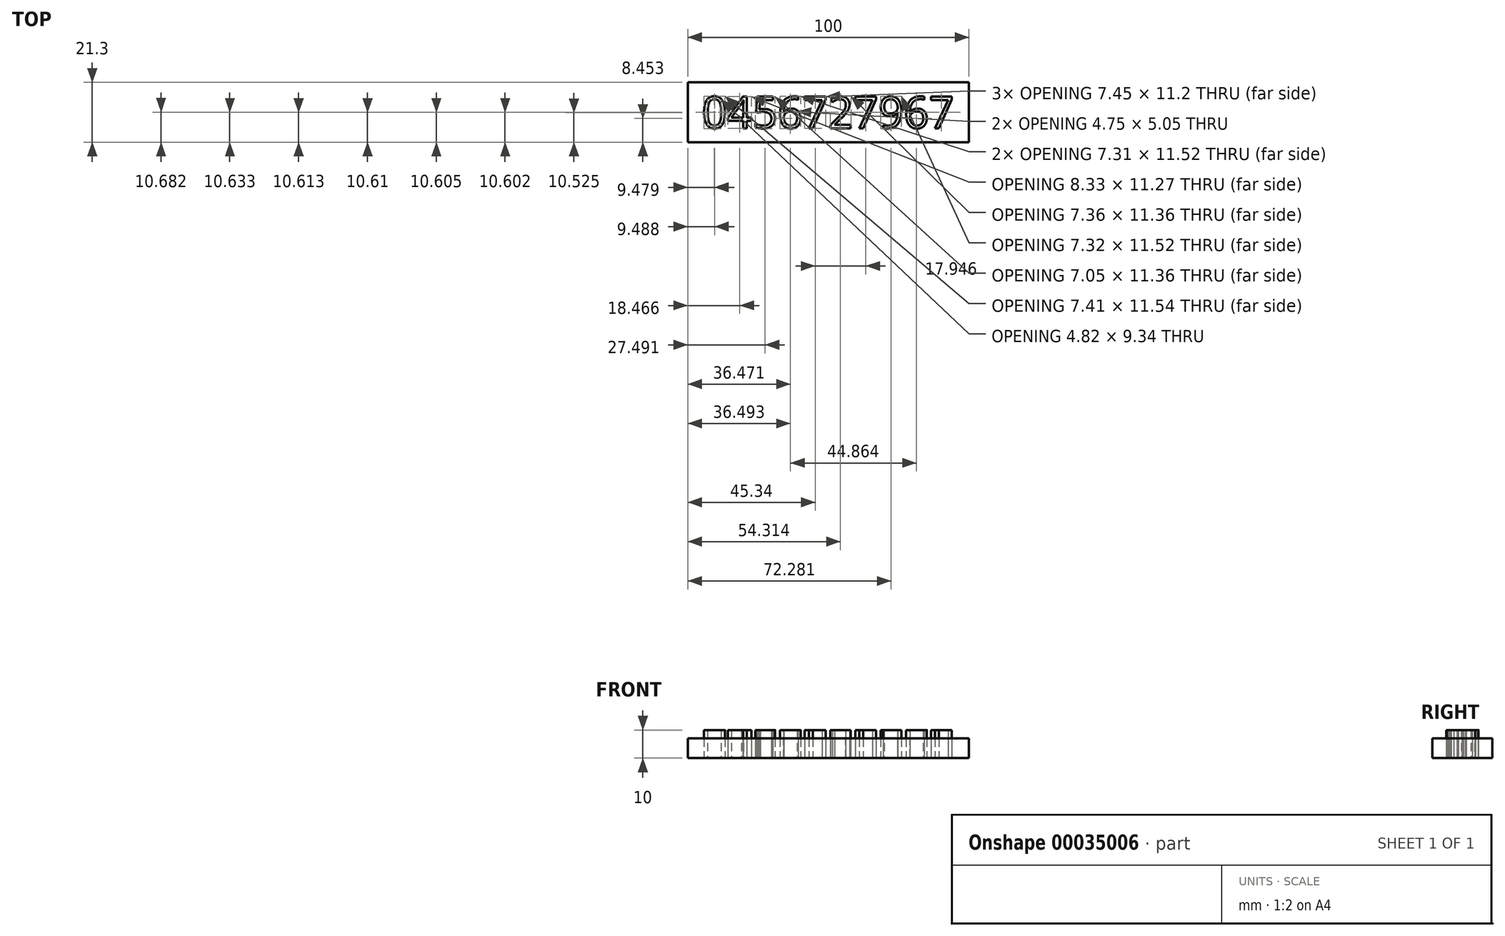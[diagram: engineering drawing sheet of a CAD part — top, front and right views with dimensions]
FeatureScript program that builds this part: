
annotation { "Feature Type Name" : "Feature", "Feature Type Description" : "" }
export const myFeature = defineFeature(function(context is Context, id is Id, definition is map)
    precondition{}
    {
        {
            var Q0;
            Q0=qCreatedBy(makeId("Top.planeOp"),FACE);
            var sketch = newSketch(context, id + "F0", { "sketchPlane" : qUnion([Q0])});
            skText(sketch, "E0", { "text": "0456727967", "fontName": "OpenSans-Regular.ttf"});
            skLineSegment(sketch, "E1.bottom", {"start": v(-50, 10.65) * mm, "end": v(50, 10.65) * mm});
            skLineSegment(sketch, "E1.top", {"start": v(-50, -10.65) * mm, "end": v(50, -10.65) * mm});
            skLineSegment(sketch, "E1.left", {"start": v(-50, 10.65) * mm, "end": v(-50, -10.65) * mm});
            skLineSegment(sketch, "E1.right", {"start": v(50, 10.65) * mm, "end": v(50, -10.65) * mm});
            skPoint(sketch, "E1.middle", {"position": v(0, 0) * mm});
            const initialGuessF0  = {"E0": [-0.045, -0.00565, 1, 0, 0.0113]};
            skSetInitialGuess(sketch, initialGuessF0);
            skSolve(sketch);
        }
        {
            var Q0;
            Q0=makeQuery(id+"F0.imprint","IMPRINT",FACE,{"disambiguationData":[TD([[makeQuery(id+"F0.imprint","IMPRINT",EDGE,{"derivedFrom":sQuery(id+"F0.wireOp",EDGE,"E0.sketch_text.stroke-52")}),-1.0]])]});
            var Q1;
            Q1=makeQuery(id+"F0.imprint","IMPRINT",FACE,{"disambiguationData":[TD([[makeQuery(id+"F0.imprint","IMPRINT",EDGE,{"derivedFrom":sQuery(id+"F0.wireOp",EDGE,"E0.sketch_text.stroke-16")}),-1.0]])]});
            var Q2;
            Q2=makeQuery(id+"F0.imprint","IMPRINT",FACE,{"disambiguationData":[TD([[makeQuery(id+"F0.imprint","IMPRINT",EDGE,{"derivedFrom":sQuery(id+"F0.wireOp",EDGE,"E0.sketch_text.stroke-0")}),-1.0]])]});
            var Q3;
            Q3=makeQuery(id+"F0.imprint","IMPRINT",FACE,{"disambiguationData":[TD([[makeQuery(id+"F0.imprint","IMPRINT",EDGE,{"derivedFrom":sQuery(id+"F0.wireOp",EDGE,"E0.sketch_text.stroke-104")}),-1.0]])]});
            var Q4;
            Q4=makeQuery(id+"F0.imprint","IMPRINT",FACE,{"disambiguationData":[TD([[makeQuery(id+"F0.imprint","IMPRINT",EDGE,{"derivedFrom":sQuery(id+"F0.wireOp",EDGE,"E0.sketch_text.stroke-33")}),-1.0]])]});
            var Q5;
            Q5=makeQuery(id+"F0.imprint","IMPRINT",FACE,{"disambiguationData":[TD([[makeQuery(id+"F0.imprint","IMPRINT",EDGE,{"derivedFrom":sQuery(id+"F0.wireOp",EDGE,"E0.sketch_text.stroke-162")}),-1.0]])]});
            var Q6;
            Q6=makeQuery(id+"F0.imprint","IMPRINT",FACE,{"disambiguationData":[TD([[makeQuery(id+"F0.imprint","IMPRINT",EDGE,{"derivedFrom":sQuery(id+"F0.wireOp",EDGE,"E0.sketch_text.stroke-137")}),-1.0]])]});
            var Q7;
            Q7=makeQuery(id+"F0.imprint","IMPRINT",FACE,{"disambiguationData":[TD([[makeQuery(id+"F0.imprint","IMPRINT",EDGE,{"derivedFrom":sQuery(id+"F0.wireOp",EDGE,"E0.sketch_text.stroke-111")}),-1.0]])]});
            var Q8;
            Q8=makeQuery(id+"F0.imprint","IMPRINT",FACE,{"disambiguationData":[TD([[makeQuery(id+"F0.imprint","IMPRINT",EDGE,{"derivedFrom":sQuery(id+"F0.wireOp",EDGE,"E0.sketch_text.stroke-77")}),-1.0]])]});
            var Q9;
            Q9=makeQuery(id+"F0.imprint","IMPRINT",FACE,{"disambiguationData":[TD([[makeQuery(id+"F0.imprint","IMPRINT",EDGE,{"derivedFrom":sQuery(id+"F0.wireOp",EDGE,"E0.sketch_text.stroke-84")}),-1.0]])]});
            extrude(context, id + "F1", {"entities" : qUnion([Q0, Q1, Q2, Q3, Q4, Q5, Q6, Q7, Q8, Q9]), "depth" : 10 * mm});
        }
        {
            var Q0;
            Q0 = qSketchRegion(id + "F0", true);
            extrude(context, id + "F2", {"entities" : qUnion([Q0]), "depth" : 7 * mm});
        }
    });
